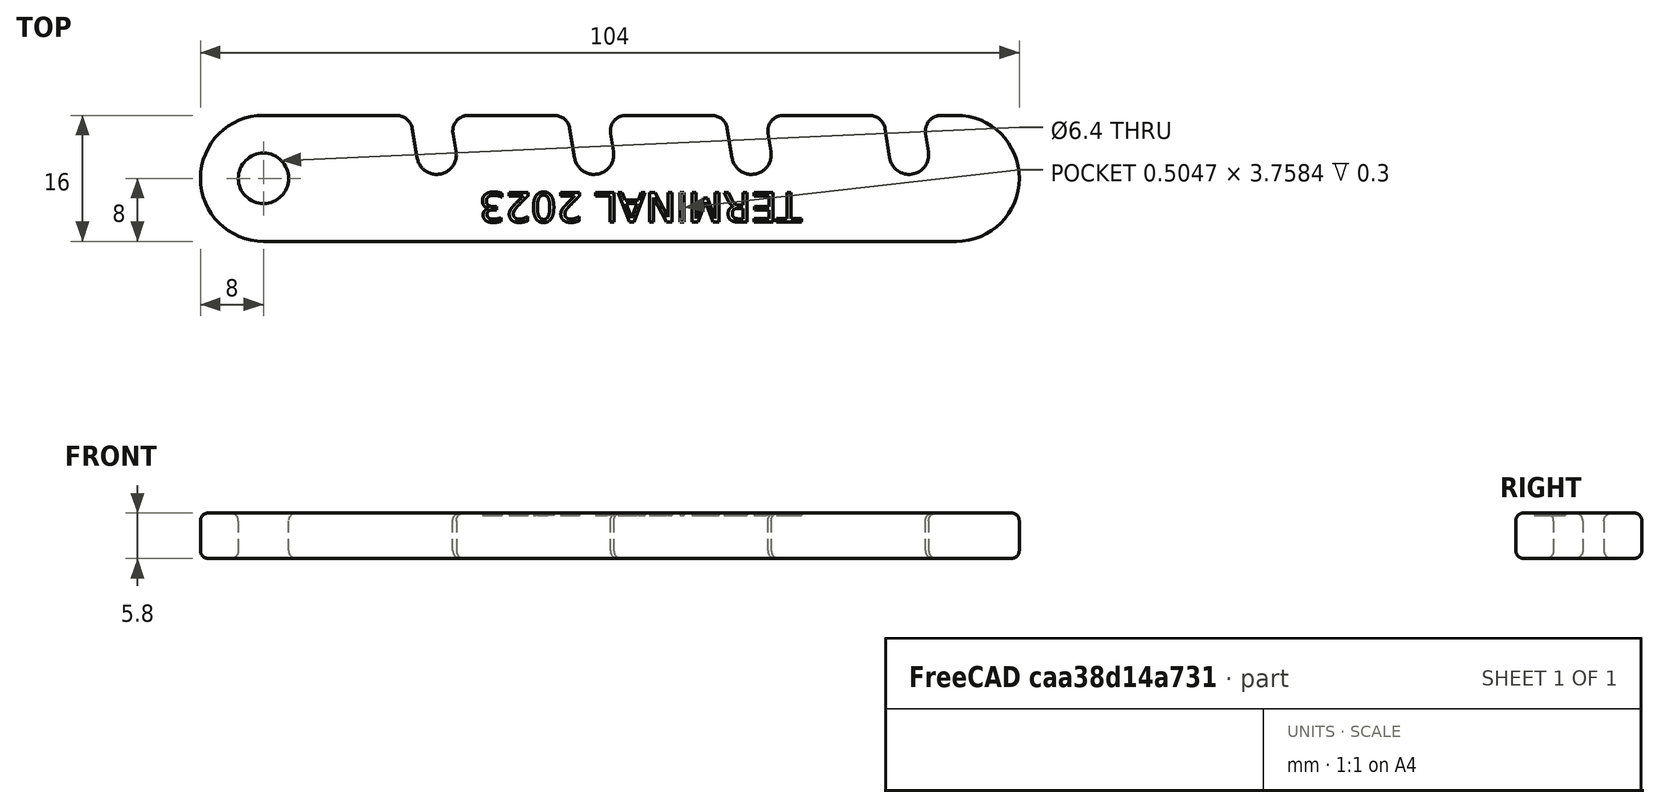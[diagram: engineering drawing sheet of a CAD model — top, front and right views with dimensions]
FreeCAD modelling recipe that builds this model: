
FCSTD DOCUMENT  (FreeCAD 0.21R33668 +26 (Git))
Label: ogranichitel-2
License: All rights reserved
LicenseURL: http://en.wikipedia.org/wiki/All_rights_reserved
objects: PartDesign::Fillet×3, Sketcher::SketchObject×1, PartDesign::Pad×1, Part::Part2DObjectPython×1, PartDesign::Pocket×1, PartDesign::Body×1
note: 13 computed .brp shape members not serialized (recipe doc carries the construction recipe); baked Part::Feature solids carry a one-line shape summary decoded from their .brp

FEATURE [Sketcher::SketchObject] Sketch
  FullyConstrained = false
  MapMode = 5
  Support = -> [XY_Plane]
  sketch-geometry (21):
    g0: ArcOfCircle CenterX=-40 CenterY=0 CenterZ=0 NormalX=0 NormalY=0 NormalZ=1 AngleXU=0 Radius=8 StartAngle=1.5708 EndAngle=4.71239
    g1: ArcOfCircle CenterX=48 CenterY=0 CenterZ=0 NormalX=0 NormalY=0 NormalZ=1 AngleXU=0 Radius=8 StartAngle=4.71239 EndAngle=7.85398
    g2: LineSegment StartX=-40 StartY=-8 StartZ=0 EndX=48 EndY=-8 EndZ=0
    g3: LineSegment StartX=48 StartY=8 StartZ=0 EndX=43.7559 EndY=8 EndZ=0
    g4: ArcOfCircle CenterX=-18 CenterY=3 CenterZ=0 NormalX=0 NormalY=0 NormalZ=1 AngleXU=0 Radius=2.5 StartAngle=3.31255 EndAngle=6.45415
    g5: LineSegment StartX=-21.4002 StartY=8 StartZ=0 EndX=-20.4636 EndY=2.57468 EndZ=0
    g6: LineSegment StartX=-15.5364 StartY=3.42532 StartZ=0 EndX=-16.3262 EndY=8 EndZ=0
    g7: ArcOfCircle CenterX=2 CenterY=3 CenterZ=0 NormalX=0 NormalY=0 NormalZ=1 AngleXU=0 Radius=2.5 StartAngle=3.30645 EndAngle=6.44804
    g8: LineSegment StartX=-1.3662 StartY=8 StartZ=0 EndX=-0.466105 EndY=2.58972 EndZ=0
    g9: LineSegment StartX=4.4661 StartY=3.41028 StartZ=0 EndX=3.70253 EndY=8 EndZ=0
    g10: ArcOfCircle CenterX=22 CenterY=3 CenterZ=0 NormalX=0 NormalY=0 NormalZ=1 AngleXU=0 Radius=2.5 StartAngle=3.30644 EndAngle=6.44804
    g11: LineSegment StartX=18.6338 StartY=8 StartZ=0 EndX=19.5339 EndY=2.58974 EndZ=0
    g12: LineSegment StartX=24.4661 StartY=3.41026 StartZ=0 EndX=23.7026 EndY=8 EndZ=0
    g13: ArcOfCircle CenterX=42 CenterY=3 CenterZ=0 NormalX=0 NormalY=0 NormalZ=1 AngleXU=0 Radius=2.5 StartAngle=3.29516 EndAngle=6.43675
    g14: LineSegment StartX=38.6963 StartY=8 StartZ=0 EndX=39.5294 EndY=2.6176 EndZ=0
    g15: LineSegment StartX=44.4706 StartY=3.3824 StartZ=0 EndX=43.7559 EndY=8 EndZ=0
    g16: Circle CenterX=-40 CenterY=0 CenterZ=0 NormalX=0 NormalY=0 NormalZ=1 AngleXU=0 Radius=3.2
    g17: LineSegment StartX=-21.4002 StartY=8 StartZ=0 EndX=-40 EndY=8 EndZ=0
    g18: LineSegment StartX=-1.3662 StartY=8 StartZ=0 EndX=-16.3262 EndY=8 EndZ=0
    g19: LineSegment StartX=18.6338 StartY=8 StartZ=0 EndX=3.70253 EndY=8 EndZ=0
    g20: LineSegment StartX=38.6963 StartY=8 StartZ=0 EndX=23.7026 EndY=8 EndZ=0
  constraints (31):
    c: Tangent(g0,g2) = -1.5708
    c: Tangent(g2,g1) = -1.5708
    c: Tangent(g1,g3) = -1.5708
    c: Coincident(g17,g0) = -1.5708
    c: PointOnObject(g0,g-1)
    c: PointOnObject(g1,g-1)
    c: Horizontal(g2)
    c: DistanceY(g1,g1) = 16
    c: DistanceX(g0,g1) = 88
    c: Tangent(g5,g4) = -1.5708
    c: Tangent(g4,g6) = -1.5708
    c: Distance(g4,g4) = 2.5
    c: Tangent(g8,g7) = -1.5708
    c: Tangent(g7,g9) = -1.5708
    c: Distance(g7,g7) = 2.5
    c: Tangent(g11,g10) = -1.5708
    c: Tangent(g10,g12) = -1.5708
    c: Distance(g10,g10) = 2.5
    c: Tangent(g14,g13) = -1.5708
    c: Tangent(g13,g15) = -1.5708
    c: Distance(g13,g13) = 2.5
    c: Coincident(g16,g0)
    c: Diameter(g16) = 6.4
    c: Coincident(g18,g6)
    c: Coincident(g17,g5)
    c: Coincident(g19,g9)
    c: Coincident(g18,g8)
    c: Coincident(g20,g12)
    c: Coincident(g19,g11)
    c: Coincident(g3,g15)
    c: Coincident(g20,g14)
FEATURE [PartDesign::Pad] Pad
  Direction = (0,0,1)
  Length = 5.8
  Length2 = 10
  Profile = -> Sketch
  ReferenceAxis = -> Sketch [N_Axis]
  Type = 0
FEATURE [PartDesign::Fillet] Fillet
  Base = -> Pad [Edge1,Edge50,Edge47,Edge38,Edge35,Edge26,Edge23,Edge14]
  BaseFeature = -> Pad
  Radius = 2
  SupportTransform = false
  UseAllEdges = false
FEATURE [PartDesign::Fillet] Fillet001
  Base = -> Fillet [Face5]
  BaseFeature = -> Fillet
  Radius = 1
  SupportTransform = false
  UseAllEdges = false
FEATURE [PartDesign::Fillet] Fillet002
  Base = -> Fillet001 [Face4]
  BaseFeature = -> Fillet001
  Radius = 1
  SupportTransform = false
  UseAllEdges = false
FEATURE [Part::Part2DObjectPython] ShapeString  # Draft 2D object (typed FeaturePython)
  FontFile = <path>
  MakeFace = true
  Placement = pos=(28.35,-1.8,7) rot=(0,0,1;3.14159rad)
  Size = 4
  String = TERMINAL 2023
  Tracking = 0
FEATURE [PartDesign::Pocket] Pocket
  BaseFeature = -> Fillet002
  Direction = (0,0,-1)
  Length = 1.5
  Length2 = 5
  Profile = -> ShapeString
  ReferenceAxis = -> ShapeString [N_Axis]
  Type = 0
FEATURE [PartDesign::Body] Body  label="Тело"
  Group = -> [Sketch,Pad,Fillet,Fillet001,Fillet002,ShapeString,Pocket]
  Origin = -> Origin
  Tip = -> Pocket
note: 1 file-system path scrubbed to <path> (originals preserved in the JSON sidecar)
